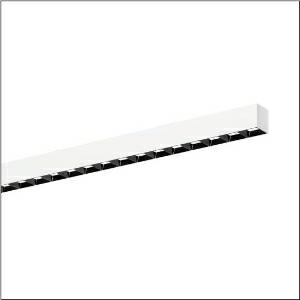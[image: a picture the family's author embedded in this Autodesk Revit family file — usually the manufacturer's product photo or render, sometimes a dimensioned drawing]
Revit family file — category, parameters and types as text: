
# Revit family: silica_r__21_51mx22tbt5w_cdcc
name_source: partatom
category: Lighting Fixtures
units: mm (PartAtom-declared; Revit-internal decimal feet)

## family parameters
Cut with Voids When Loaded = No
Host = Face
Light Source = No
Part Type = Normal
Room Calculation Point = No
Round Connector Dimension = Use Diameter
Shared = No

## types (1)
- --- (1 x LED, 4650 lm, 40.2 W, 6500K)
    Apparent Load = 40 VA
    CIE Flux Codes = 84 100 100 100 100
    Color Rendering = 80
    Color Temperature = 6500K
    Default Elevation = 1800 mm
    Description = Silica® 21, office luminaire, primary light control with darklight reflector, of PMMA, black, CAT 2 (L<= 3000cd/m²), light emission: direct distribution, primary light characteristic: symmetric, installation type: surface-mounted, LED, rated luminous flux: 4.650lm, luminous efficacy: 110lm/W, light colour: 8tw, colour temperature: 2700..6500K, control gear: DALI DT8, with terminal, 3+2-pole, max. 2.5mm², mains connection: 220..240V, AC, 50/60Hz, rated input power: 42.2W, luminaire housing, of aluminium, traffic white (RAL 9016), length: 1.504mm, width: 53mm, height: 53mm, protection rating (complete): IP20, insulation class (complete): insulation class I (protective earthing), certification: CE, permissible operating ambient temperature: 0..+35°C, standard: EN 50419, packaging unit: 1 piece
    Height = 53 mm
    Lamp = 1 x LED
    Lamp Light Flux = 4650 lm
    Lamp Power = 40.2 W
    Lamp count = 1
    Length = 1504 mm
    Luminous efficacy = 116 lm/W
    Manufacturer = Siteco
    ModVariant = No
    Model = 51MX22TBT5W
    Mounting Place = Ceiling
    Mounting Type = Surface mounted
    Number of Poles = 1
    OnlyDefault = Yes
    Power Factor = 1
    Product Name = Silica® 21
    Product group = office luminaire | ceiling mounted
    ProductGroupID = 302
    Protection Class = Protection class I
    Protection Degree = IP 20
    RLX_Detail_Level = 1
    RLX_Emergency_Light_Flux = 0 lm
    RLX_Emergency_Type = 0
    RLX_Emergency_Type_DB = No
    RlxData = <blob elided: 41205 chars, md5=0e4d93de>
    Socket = socket
    Standby Power = 0 W
    System Light Flux = 4650 lm
    System Power = 40 W
    Type Comments = individual setting
    Type Image = l_1335873.jpg
    URL = http://relux.com
    VarID = @adj_140154
    Voltage = 0 V
    Weight = 0.00 kg
    Width = 53 mm

## geometry (parser evidence)
native form markers: Blend x4, Sweep x11
no freeform markers — native parametric forms only
